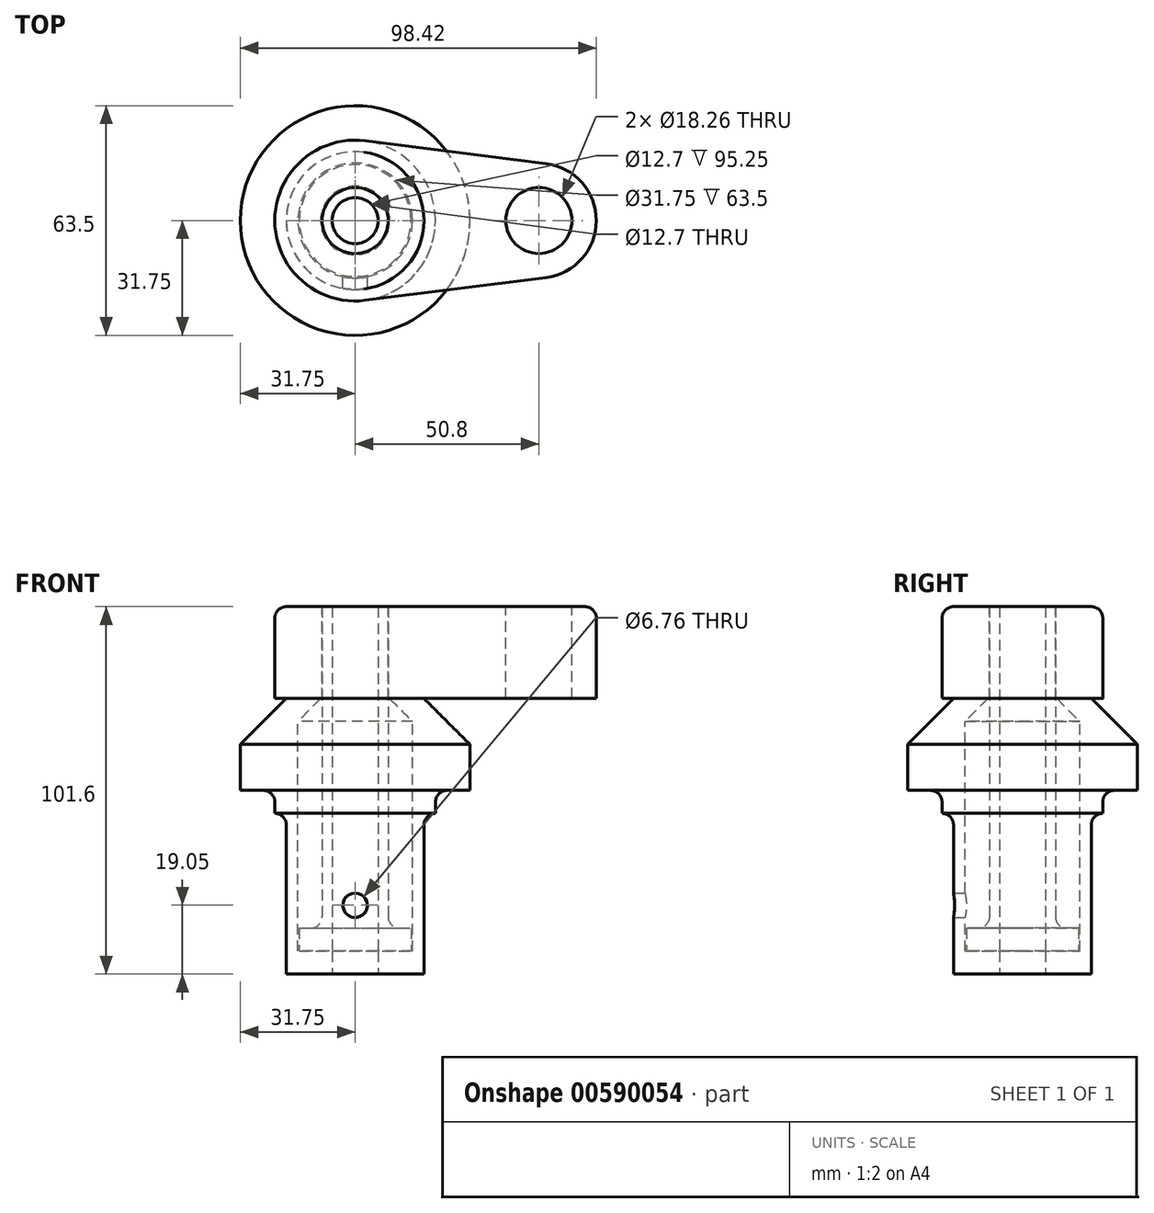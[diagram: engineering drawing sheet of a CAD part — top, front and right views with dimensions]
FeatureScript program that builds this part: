
annotation { "Feature Type Name" : "Feature", "Feature Type Description" : "" }
export const myFeature = defineFeature(function(context is Context, id is Id, definition is map)
    precondition{}
    {
        {
            var Q0;
            Q0=qCreatedBy(makeId("Front.planeOp"),FACE);
            var sketch = newSketch(context, id + "F0", { "sketchPlane" : qUnion([Q0])});
            skLineSegment(sketch, "E0", {"start": v(0, 0) * mm, "end": v(0, 76.2) * mm});
            skLineSegment(sketch, "E1", {"start": v(0, 76.2) * mm, "end": v(19.05, 76.2) * mm});
            skLineSegment(sketch, "E2", {"start": v(19.05, 76.2) * mm, "end": v(31.75, 63.5) * mm});
            skLineSegment(sketch, "E3", {"start": v(31.75, 63.5) * mm, "end": v(31.75, 50.8) * mm});
            skLineSegment(sketch, "E4", {"start": v(31.75, 50.8) * mm, "end": v(22.23, 50.8) * mm});
            skLineSegment(sketch, "E5", {"start": v(22.23, 50.8) * mm, "end": v(22.23, 44.45) * mm});
            skLineSegment(sketch, "E6", {"start": v(22.23, 44.45) * mm, "end": v(19.05, 44.45) * mm});
            skLineSegment(sketch, "E7", {"start": v(19.05, 44.45) * mm, "end": v(19.05, 0) * mm});
            skLineSegment(sketch, "E8", {"start": v(19.05, 0) * mm, "end": v(0, 0) * mm});
            skLineSegment(sketch, "E9", {"start": v(9.52, 76.2) * mm, "end": v(15.88, 69.85) * mm});
            skLineSegment(sketch, "E10", {"start": v(15.88, 69.85) * mm, "end": v(15.88, 6.35) * mm});
            skLineSegment(sketch, "E11", {"start": v(15.88, 6.35) * mm, "end": v(0, 6.35) * mm});
            skLineSegment(sketch, "E12", {"start": v(0, 76.2) * mm, "end": v(0, 87.13) * mm, "construction": true});
            skLineSegment(sketch, "E13", {"start": v(0, 76.2) * mm, "end": v(0, 101.6) * mm});
            skLineSegment(sketch, "E14", {"start": v(0, 101.6) * mm, "end": v(9.13, 101.6) * mm});
            skLineSegment(sketch, "E15", {"start": v(9.13, 101.6) * mm, "end": v(9.13, 12.7) * mm});
            skLineSegment(sketch, "E16", {"start": v(9.13, 12.7) * mm, "end": v(15.48, 12.7) * mm});
            skLineSegment(sketch, "E17", {"start": v(15.48, 12.7) * mm, "end": v(15.48, 6.35) * mm});
            skSolve(sketch);
        }
        {
            var Q0;
            {var subQ4=sQuery(id+"F0.wireOp",EDGE,"E2");Q0=makeQuery(id+"F0.imprint","IMPRINT",FACE,{"disambiguationData":[TD([[makeQuery(id+"F0.imprint","IMPRINT",EDGE,{"derivedFrom":subQ4}),-1.0]])]});}
            var Q1;
            Q1=sQuery(id+"F0.wireOp",EDGE,"E0");
            revolve(context, id + "F1", {"entities" : qUnion([Q0]), "axis" : qUnion([Q1]), "revolveType" : RevolveType.FULL, "oppositeDirection" : true});
        }
        {
            var Q0;
            {var subQ0=sQuery(id+"F0.wireOp",EDGE,"E13");Q0=makeQuery(id+"F0.imprint","IMPRINT",FACE,{"disambiguationData":[TD([[makeQuery(id+"F0.imprint","IMPRINT",EDGE,{"derivedFrom":subQ0}),-1.0]])]});}
            var Q1;
            {var subQ0=sQuery(id+"F0.wireOp",EDGE,"E16");Q1=makeQuery(id+"F0.imprint","IMPRINT",FACE,{"disambiguationData":[TD([[makeQuery(id+"F0.imprint","IMPRINT",EDGE,{"derivedFrom":subQ0}),-1.0]])]});}
            var Q2;
            Q2=sQuery(id+"F0.wireOp",EDGE,"E13");
            revolve(context, id + "F2", {"entities" : qUnion([Q0, Q1]), "axis" : qUnion([Q2]), "revolveType" : RevolveType.FULL});
        }
        {
            var Q0;
            Q0=makeQuery(id+"F2.opRevolve","SWEPT_FACE",FACE,{"disambiguationData":[OSD([sQuery(id+"F0.wireOp",EDGE,"E14")])]});
            var sketch = newSketch(context, id + "F3", { "sketchPlane" : qUnion([Q0])});
            skCircle(sketch, "E18", {"center": v(0, 0) * mm, "radius": 22.23 * mm});
            skCircle(sketch, "E19", {"center": v(50.8, 0) * mm, "radius": 15.88 * mm});
            skLineSegment(sketch, "E20", {"start": v(2.78, 22.05) * mm, "end": v(52.78, 15.75) * mm});
            skLineSegment(sketch, "E21", {"start": v(52.78, -15.75) * mm, "end": v(2.78, -22.05) * mm});
            skCircle(sketch, "E22.0", {"center": v(0, 0) * mm, "radius": 9.13 * mm});
            skCircle(sketch, "E23", {"center": v(50.8, 0) * mm, "radius": 9.13 * mm});
            skSolve(sketch);
        }
        {
            var Q0;
            Q0 = qSketchRegion(id + "F3", true);
            var Q1;
            Q1=makeQuery(id+"F1.opRevolve","SWEPT_FACE",FACE,{"disambiguationData":[OSD([sQuery(id+"F0.wireOp",EDGE,"E1")])]});
            extrude(context, id + "F4", {"entities" : qUnion([Q0]), "oppositeDirection" : true, "depth" : 25.4 * mm, "endBoundEntityFace" : qUnion([Q1]), "offsetDistance" : 1.59 * mm});
        }
        {
            var Q0;
            Q0=qCreatedBy(makeId("Front.planeOp"),FACE);
            var sketch = newSketch(context, id + "F5", { "sketchPlane" : qUnion([Q0])});
            skPoint(sketch, "E24", {"position": v(0, 19.05) * mm});
            skSolve(sketch);
        }
        {
            var Q0;
            Q0=sQuery(id+"F5.wireOp",VERTEX,"E24");
            var Q1;
            Q1=makeQuery(id+"F1.opRevolve","SWEPT_BODY",BODY,{"disambiguationData":[OSD([sQuery(id+"F0.wireOp",EDGE,"E0"),sQuery(id+"F0.wireOp",EDGE,"E1"),sQuery(id+"F0.wireOp",EDGE,"E2"),sQuery(id+"F0.wireOp",EDGE,"E3"),sQuery(id+"F0.wireOp",EDGE,"E4"),sQuery(id+"F0.wireOp",EDGE,"E5"),sQuery(id+"F0.wireOp",EDGE,"E6"),sQuery(id+"F0.wireOp",EDGE,"E7"),sQuery(id+"F0.wireOp",EDGE,"E8"),sQuery(id+"F0.wireOp",EDGE,"E9"),sQuery(id+"F0.wireOp",EDGE,"E10"),sQuery(id+"F0.wireOp",EDGE,"E11")])]});
            hole(context, id + "F6", {"style" : HoleStyle.SIMPLE, "endStyle" : HoleEndStyle.THROUGH, "oppositeDirection" : true, "standardTappedOrClearance" : lookupTablePath({ "standard" : "ANSI", "fit" : "Normal (ASME)", "size" : "1/4", "type" : "Clearance" }), "standardBlindInLast" : lookupTablePath({ "fit" : "Free", "standard" : "ANSI", "size" : "1/4", "type" : "Clearance" }), "holeDiameter" : 6.76 * mm, "majorDiameter" : 6.35 * mm, "tappedDepth" : 14.3 * mm, "tapClearance" : 3, "locations" : qUnion([Q0]), "scope" : qUnion([Q1])});
        }
        {
            var Q0;
            Q0=makeQuery(id+"F4.opExtrude","CAP_EDGE",EDGE,{"disambiguationData":[OSD([sQuery(id+"F3.wireOp",EDGE,"E18")])],"isStart":true});
            var Q1;
            Q1=makeQuery(id+"F1.opRevolve","SWEPT_EDGE",EDGE,{"disambiguationData":[OSD([sQuery(id+"F0.wireOp",EDGE,"E6"),sQuery(id+"F0.wireOp",EDGE,"E7")])]});
            var Q2;
            Q2=makeQuery(id+"F1.opRevolve","SWEPT_EDGE",EDGE,{"disambiguationData":[OSD([sQuery(id+"F0.wireOp",EDGE,"E4"),sQuery(id+"F0.wireOp",EDGE,"E5")])]});
            var Q3;
            Q3=makeQuery(id+"F2.opRevolve","SWEPT_EDGE",EDGE,{"disambiguationData":[OSD([sQuery(id+"F0.wireOp",EDGE,"E15"),sQuery(id+"F0.wireOp",EDGE,"E16")])]});
            fillet(context, id + "F7", {"entities" : qUnion([Q0, Q1, Q2, Q3]), "radius" : 3.17 * mm, "tangentPropagation" : true, "allowEdgeOverflow" : false});
        }
        {
            var Q0;
            Q0=makeQuery(id+"F1.opRevolve","SWEPT_FACE",FACE,{"disambiguationData":[OSD([sQuery(id+"F0.wireOp",EDGE,"E8")])]});
            var sketch = newSketch(context, id + "F8", { "sketchPlane" : qUnion([Q0])});
            skCircle(sketch, "E25", {"center": v(0, 0) * mm, "radius": 6.35 * mm});
            skSolve(sketch);
        }
        {
            var Q0;
            Q0 = qSketchRegion(id + "F8", true);
            extrude(context, id + "F9", {"entities" : qUnion([Q0]), "operationType" : NewBodyOperationType.REMOVE, "endBound" : BoundingType.THROUGH_ALL, "oppositeDirection" : true, "depth" : 25.4 * mm, "offsetDistance" : 25.4 * mm});
        }
    });
